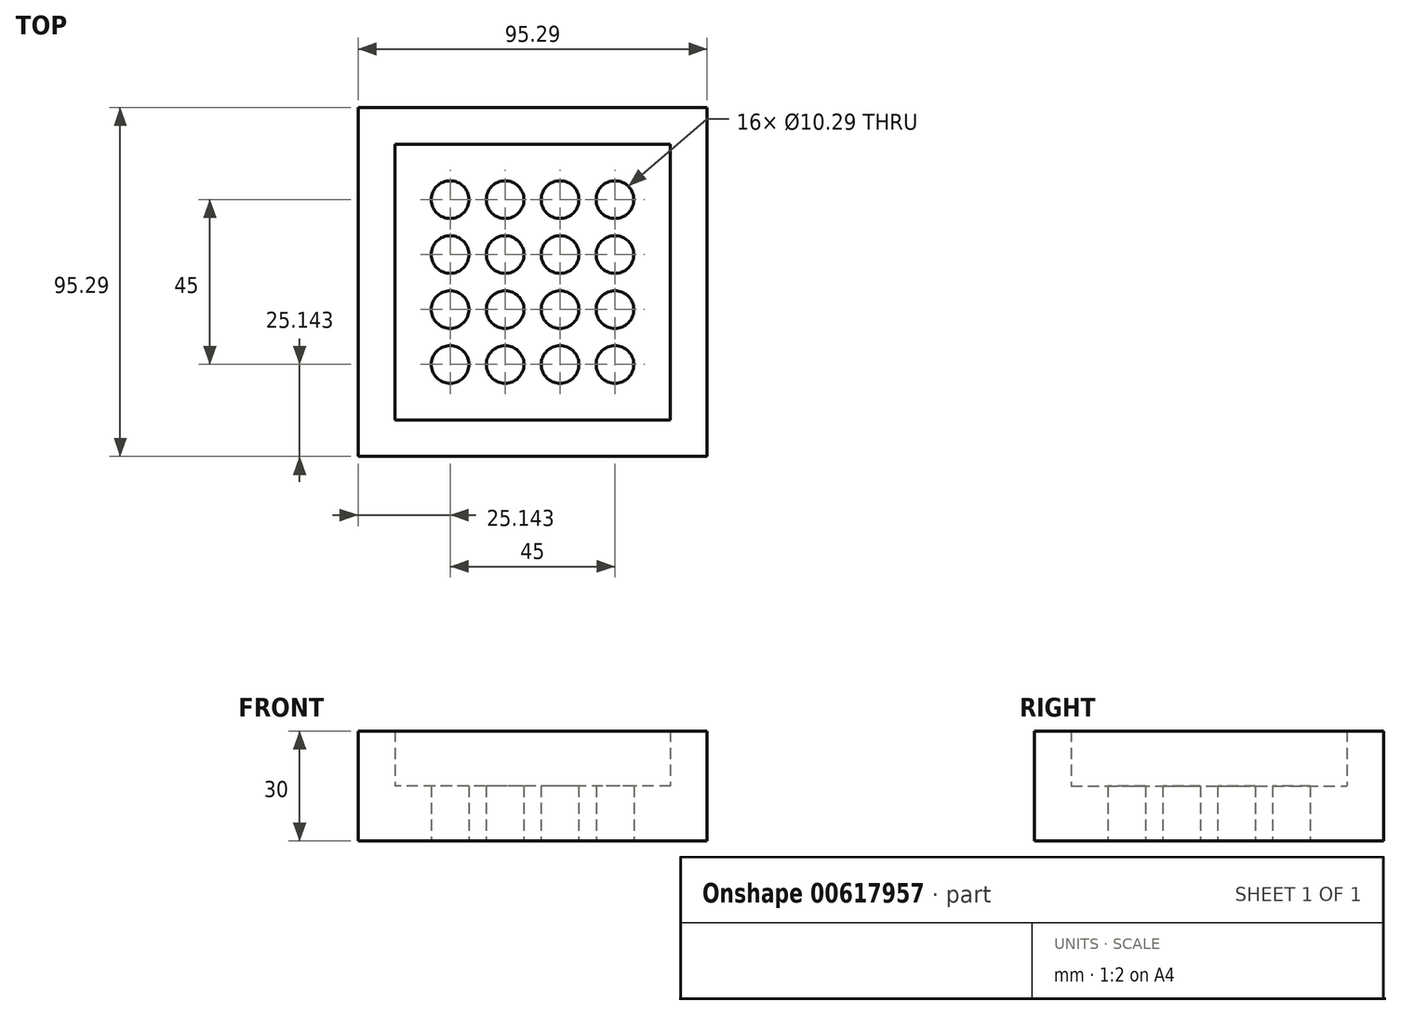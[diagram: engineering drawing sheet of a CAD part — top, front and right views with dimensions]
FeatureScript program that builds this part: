
annotation { "Feature Type Name" : "Feature", "Feature Type Description" : "" }
export const myFeature = defineFeature(function(context is Context, id is Id, definition is map)
    precondition{}
    {
        {
            var Q0;
            Q0=qCreatedBy(makeId("Top.planeOp"),FACE);
            var sketch = newSketch(context, id + "F0", { "sketchPlane" : qUnion([Q0])});
            skCircle(sketch, "E0", {"center": v(25.14, 25.14) * mm, "radius": 5.14 * mm});
            skCircle(sketch, "E1.0.1.0", {"center": v(25.14, 40.14) * mm, "radius": 5.14 * mm});
            skCircle(sketch, "E1.0.2.0", {"center": v(25.14, 55.14) * mm, "radius": 5.14 * mm});
            skCircle(sketch, "E1.0.3.0", {"center": v(25.14, 70.14) * mm, "radius": 5.14 * mm});
            skCircle(sketch, "E1.1.0.0", {"center": v(40.14, 25.14) * mm, "radius": 5.14 * mm});
            skCircle(sketch, "E1.1.1.0", {"center": v(40.14, 40.14) * mm, "radius": 5.14 * mm});
            skCircle(sketch, "E1.1.2.0", {"center": v(40.14, 55.14) * mm, "radius": 5.14 * mm});
            skCircle(sketch, "E1.1.3.0", {"center": v(40.14, 70.14) * mm, "radius": 5.14 * mm});
            skCircle(sketch, "E1.2.0.0", {"center": v(55.14, 25.14) * mm, "radius": 5.14 * mm});
            skCircle(sketch, "E1.2.1.0", {"center": v(55.14, 40.14) * mm, "radius": 5.14 * mm});
            skCircle(sketch, "E1.2.2.0", {"center": v(55.14, 55.14) * mm, "radius": 5.14 * mm});
            skCircle(sketch, "E1.2.3.0", {"center": v(55.14, 70.14) * mm, "radius": 5.14 * mm});
            skCircle(sketch, "E1.3.0.0", {"center": v(70.14, 25.14) * mm, "radius": 5.14 * mm});
            skCircle(sketch, "E1.3.1.0", {"center": v(70.14, 40.14) * mm, "radius": 5.14 * mm});
            skCircle(sketch, "E1.3.2.0", {"center": v(70.14, 55.14) * mm, "radius": 5.14 * mm});
            skCircle(sketch, "E1.3.3.0", {"center": v(70.14, 70.14) * mm, "radius": 5.14 * mm});
            skLineSegment(sketch, "E1.direction1", {"start": v(25.14, 25.14) * mm, "end": v(40.14, 25.14) * mm, "construction": true});
            skLineSegment(sketch, "E1.direction2", {"start": v(25.14, 25.14) * mm, "end": v(25.14, 40.14) * mm, "construction": true});
            skLineSegment(sketch, "E2.bottom", {"start": v(0, 0) * mm, "end": v(95.29, 0) * mm});
            skLineSegment(sketch, "E2.top", {"start": v(0, 95.29) * mm, "end": v(95.29, 95.29) * mm});
            skLineSegment(sketch, "E2.left", {"start": v(0, 0) * mm, "end": v(0, 95.29) * mm});
            skLineSegment(sketch, "E2.right", {"start": v(95.29, 0) * mm, "end": v(95.29, 95.29) * mm});
            skSolve(sketch);
        }
        {
            var Q0;
            Q0=makeQuery(id+"F0.imprint","IMPRINT",FACE,{"disambiguationData":[TD([[makeQuery(id+"F0.imprint","IMPRINT",EDGE,{"derivedFrom":sQuery(id+"F0.wireOp",EDGE,"E0")}),-1.0]])]});
            extrude(context, id + "F1", {"entities" : qUnion([Q0]), "depth" : 15 * mm, "offsetDistance" : 25 * mm});
        }
        {
            var Q0;
            Q0=makeQuery(id+"F1.opExtrude","CAP_FACE",FACE,{"disambiguationData":[OSD([sQuery(id+"F0.wireOp",EDGE,"E0"),sQuery(id+"F0.wireOp",EDGE,"E1.0.1.0"),sQuery(id+"F0.wireOp",EDGE,"E1.0.2.0"),sQuery(id+"F0.wireOp",EDGE,"E1.0.3.0"),sQuery(id+"F0.wireOp",EDGE,"E1.1.0.0"),sQuery(id+"F0.wireOp",EDGE,"E1.1.1.0"),sQuery(id+"F0.wireOp",EDGE,"E1.1.2.0"),sQuery(id+"F0.wireOp",EDGE,"E1.1.3.0"),sQuery(id+"F0.wireOp",EDGE,"E1.2.0.0"),sQuery(id+"F0.wireOp",EDGE,"E1.2.1.0"),sQuery(id+"F0.wireOp",EDGE,"E1.2.2.0"),sQuery(id+"F0.wireOp",EDGE,"E1.2.3.0"),sQuery(id+"F0.wireOp",EDGE,"E1.3.0.0"),sQuery(id+"F0.wireOp",EDGE,"E1.3.1.0"),sQuery(id+"F0.wireOp",EDGE,"E1.3.2.0"),sQuery(id+"F0.wireOp",EDGE,"E1.3.3.0"),sQuery(id+"F0.wireOp",EDGE,"E2.bottom"),sQuery(id+"F0.wireOp",EDGE,"E2.top"),sQuery(id+"F0.wireOp",EDGE,"E2.left"),sQuery(id+"F0.wireOp",EDGE,"E2.right")])],"isStart":false});
            var sketch = newSketch(context, id + "F2", { "sketchPlane" : qUnion([Q0])});
            skLineSegment(sketch, "E3.0", {"start": v(85.29, 85.29) * mm, "end": v(10, 85.29) * mm});
            skLineSegment(sketch, "E3.1", {"start": v(85.29, 10) * mm, "end": v(85.29, 85.29) * mm});
            skLineSegment(sketch, "E3.2", {"start": v(10, 10) * mm, "end": v(85.29, 10) * mm});
            skLineSegment(sketch, "E3.3", {"start": v(10, 85.29) * mm, "end": v(10, 10) * mm});
            skSolve(sketch);
        }
        {
            var Q0;
            Q0=makeQuery(id+"F2.imprint","IMPRINT",FACE,{"disambiguationData":[TD([[makeQuery(id+"F2.imprint","IMPRINT",EDGE,{"derivedFrom":sQuery(id+"F2.wireOp",EDGE,"E3.0")}),-1.0]])]});
            extrude(context, id + "F3", {"entities" : qUnion([Q0]), "operationType" : NewBodyOperationType.ADD, "depth" : 15 * mm, "offsetDistance" : 25 * mm});
        }
    });
